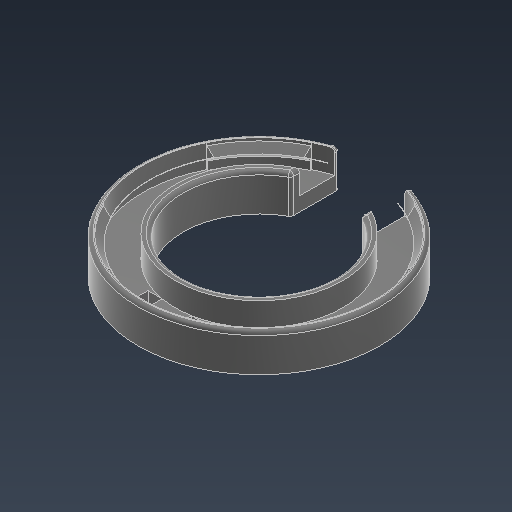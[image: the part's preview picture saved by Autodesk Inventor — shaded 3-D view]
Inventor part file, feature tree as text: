
AUTODESK INVENTOR PART (.ipt)
format: ipt  version: 2021.3 (Build 253353000, 353)  size: 332,800 bytes
history: native  units: mm
features: extrude x6, sketch x4, fillet x3, draft x1, revolve x1, direct_edit x1, other x1
ambient origin geometry x8: Origin, YZ Plane, XZ Plane, XY Plane, X Axis, Y Axis, Z Axis, Center Point
bodies: Solid1 (feature_tree)
feature tree (17):
  sketch  "Sketch1"  dims[d0=35.5mm d2=49.02mm]
  extrude  "Extrusion1"  Depth=49.02mm
  extrude  "Extrusion2"  Depth=7.0mm TaperAngle=0.0deg
  draft  "FaceDraft1"
  sketch  "Sketch2"  dims[d3=1.2mm d4=7.0mm d5=0.0mm]
  extrude  "Extrusion3"  Depth=0.401426mm
  fillet  "Fillet3"  Radius=1.6mm
  revolve  "Revolution1"  [1 undecoded]
  extrude  "Extrusion4"  Depth=6.0mm TaperAngle=0.0deg
  direct_edit  "Direct Edit3"
  extrude  "Extrusion6"  Depth=0.8mm
  extrude  "Extrusion7"  Depth=3.1mm
  fillet  "Fillet5"  Radius=3.0mm
  fillet  "Fillet6"  [1 undecoded]
  sketch  "Sketch3"  dims[d6=2.0mm d7=0.0mm d8=0.401426mm d22=1.6mm]
  sketch  "Sketch5"  dims[d23=14.9mm d24=3.0mm d25=6.0mm d26=0.0mm d27=0.8mm d29=3.1mm d30=3.0mm d31=45.0deg d32=90.0deg d33=23.1mm d34=90.0deg d35=0.0mm d36=0.0mm d40=14.9mm d49=-0.127mm d51=3.0mm d52=0.0mm d53=22.0mm d54=22.0mm d55=10.0mm d56=0.0mm d57=0.8mm d58=0.5mm]
  other  "Size1"
note: 2 required parameter values undecoded (feature->parameter linkage not recoverable at this tier; creation-order binding heuristic only, values carry confidence <= 0.55)